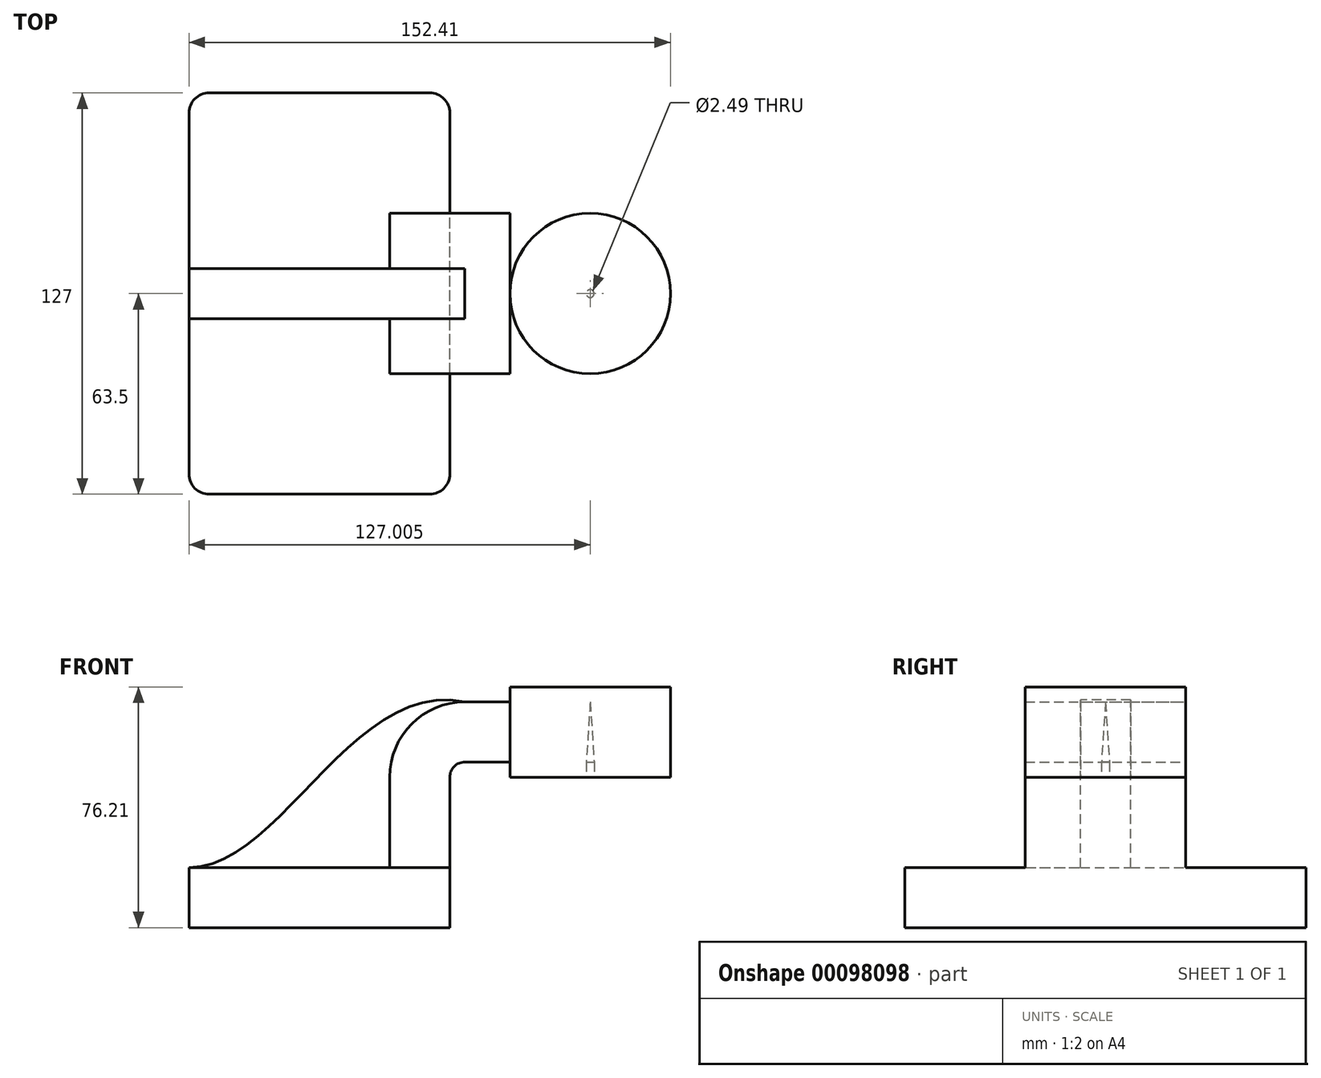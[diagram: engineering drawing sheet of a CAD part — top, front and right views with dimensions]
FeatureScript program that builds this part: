
annotation { "Feature Type Name" : "Feature", "Feature Type Description" : "" }
export const myFeature = defineFeature(function(context is Context, id is Id, definition is map)
    precondition{}
    {
        {
            var Q0;
            Q0=qCreatedBy(makeId("Front.planeOp"),FACE);
            var sketch = newSketch(context, id + "F0", { "sketchPlane" : qUnion([Q0])});
            skLineSegment(sketch, "E0.bottom", {"start": v(41.27, 9.53) * mm, "end": v(-41.28, 9.53) * mm});
            skLineSegment(sketch, "E0.top", {"start": v(41.28, -9.52) * mm, "end": v(-41.27, -9.52) * mm});
            skLineSegment(sketch, "E0.left", {"start": v(41.27, 9.53) * mm, "end": v(41.28, -9.52) * mm});
            skLineSegment(sketch, "E0.right", {"start": v(-41.28, 9.53) * mm, "end": v(-41.27, -9.52) * mm});
            skPoint(sketch, "E0.middle", {"position": v(0, 0) * mm});
            skLineSegment(sketch, "E1.bottom", {"start": v(111.12, 66.68) * mm, "end": v(60.32, 66.68) * mm});
            skLineSegment(sketch, "E1.top", {"start": v(111.12, 38.1) * mm, "end": v(60.32, 38.1) * mm});
            skLineSegment(sketch, "E1.left", {"start": v(111.12, 66.68) * mm, "end": v(111.12, 38.1) * mm});
            skLineSegment(sketch, "E1.right", {"start": v(60.32, 66.68) * mm, "end": v(60.32, 38.1) * mm});
            skPoint(sketch, "E1.middle", {"position": v(85.72, 52.39) * mm});
            skLineSegment(sketch, "E2", {"start": v(41.27, 9.53) * mm, "end": v(41.27, 38.1) * mm});
            skArc(sketch, "E3", {"start": v(46.05, 42.88) * mm, "mid": v(42.67, 41.48) * mm, "end": v(41.27, 38.1) * mm});
            skLineSegment(sketch, "E4", {"start": v(46.05, 42.88) * mm, "end": v(86.97, 42.88) * mm});
            skLineSegment(sketch, "E5", {"start": v(86.97, 42.88) * mm, "end": v(76.29, 42.88) * mm});
            skLineSegment(sketch, "E6.0", {"start": v(46.05, 61.93) * mm, "end": v(85.72, 61.93) * mm});
            skArc(sketch, "E6.1", {"start": v(46.05, 61.93) * mm, "mid": v(29.2, 54.95) * mm, "end": v(22.22, 38.1) * mm});
            skLineSegment(sketch, "E6.2", {"start": v(22.22, 9.53) * mm, "end": v(22.22, 38.1) * mm});
            skLineSegment(sketch, "E7", {"start": v(86.97, 42.88) * mm, "end": v(85.72, 61.93) * mm});
            skFitSpline(sketch, "E8", {"points": [v(-41.28, 9.52) * mm, v(46.05, 61.93) * mm], "startDerivative": vector(87.72, 0) * mm, "endDerivative": vector(107.78, -22.11) * mm});
            skPoint(sketch, "E9", {"position": v(85.72, 66.68) * mm});
            skLineSegment(sketch, "E10", {"start": v(85.72, 61.93) * mm, "end": v(85.72, 66.68) * mm});
            skLineSegment(sketch, "E11", {"start": v(86.97, 42.88) * mm, "end": v(86.97, 38.1) * mm});
            skPoint(sketch, "E11.endSnap0", {"position": v(85.72, 38.1) * mm});
            skSolve(sketch);
        }
        {
            var Q0;
            Q0=makeQuery(id+"F0.imprint","IMPRINT",FACE,{"disambiguationData":[TD([[makeQuery(id+"F0.imprint","IMPRINT",EDGE,{"derivedFrom":sQuery(id+"F0.wireOp",EDGE,"E0.top")}),-1.0]])]});
            extrude(context, id + "F1", {"entities" : qUnion([Q0]), "endBound" : BoundingType.SYMMETRIC, "depth" : 127 * mm});
        }
        {
            var Q0;
            {var subQ5=sQuery(id+"F0.wireOp",EDGE,"E2");Q0=makeQuery(id+"F0.imprint","IMPRINT",FACE,{"disambiguationData":[TD([[makeQuery(id+"F0.imprint","IMPRINT",EDGE,{"derivedFrom":subQ5}),1.0]])]});}
            var Q1;
            {var subQ4=sQuery(id+"F0.wireOp",EDGE,"E5");Q1=makeQuery(id+"F0.imprint","IMPRINT",FACE,{"disambiguationData":[TD([[makeQuery(id+"F0.imprint","IMPRINT",EDGE,{"derivedFrom":subQ4}),-1.0]])]});}
            extrude(context, id + "F2", {"entities" : qUnion([Q0, Q1]), "operationType" : NewBodyOperationType.ADD, "endBound" : BoundingType.SYMMETRIC, "depth" : 50.8 * mm});
        }
        {
            var Q0;
            Q0=makeQuery(id+"F0.imprint","IMPRINT",FACE,{"disambiguationData":[TD([[makeQuery(id+"F0.imprint","IMPRINT",EDGE,{"derivedFrom":sQuery(id+"F0.wireOp",EDGE,"E6.1")}),-1.0]])]});
            extrude(context, id + "F3", {"entities" : qUnion([Q0]), "operationType" : NewBodyOperationType.ADD, "endBound" : BoundingType.SYMMETRIC, "depth" : 15.88 * mm});
        }
        {
            var Q0;
            {var subQ0=sQuery(id+"F0.wireOp",EDGE,"E1.left");Q0=makeQuery(id+"F0.imprint","IMPRINT",FACE,{"disambiguationData":[TD([[makeQuery(id+"F0.imprint","IMPRINT",EDGE,{"derivedFrom":subQ0}),-1.0]])]});}
            var Q1;
            Q1=sQuery(id+"F0.wireOp",EDGE,"E10");
            revolve(context, id + "F4", {"operationType" : NewBodyOperationType.ADD, "entities" : qUnion([Q0]), "axis" : qUnion([Q1]), "revolveType" : RevolveType.FULL});
        }
        {
            var Q0;
            Q0=makeQuery(id+"F1.opExtrude","CAP_EDGE",EDGE,{"disambiguationData":[OSD([sQuery(id+"F0.wireOp",EDGE,"E0.right")])],"isStart":false});
            var Q1;
            Q1=makeQuery(id+"F1.opExtrude","CAP_EDGE",EDGE,{"disambiguationData":[OSD([sQuery(id+"F0.wireOp",EDGE,"E0.left")])],"isStart":false});
            var Q2;
            Q2=makeQuery(id+"F1.opExtrude","CAP_EDGE",EDGE,{"disambiguationData":[OSD([sQuery(id+"F0.wireOp",EDGE,"E0.left")])],"isStart":true});
            var Q3;
            Q3=makeQuery(id+"F1.opExtrude","CAP_EDGE",EDGE,{"disambiguationData":[OSD([sQuery(id+"F0.wireOp",EDGE,"E0.right")])],"isStart":true});
            fillet(context, id + "F5", {"entities" : qUnion([Q0, Q1, Q2, Q3]), "radius" : 6.35 * mm, "tangentPropagation" : true, "allowEdgeOverflow" : false});
        }
    });
